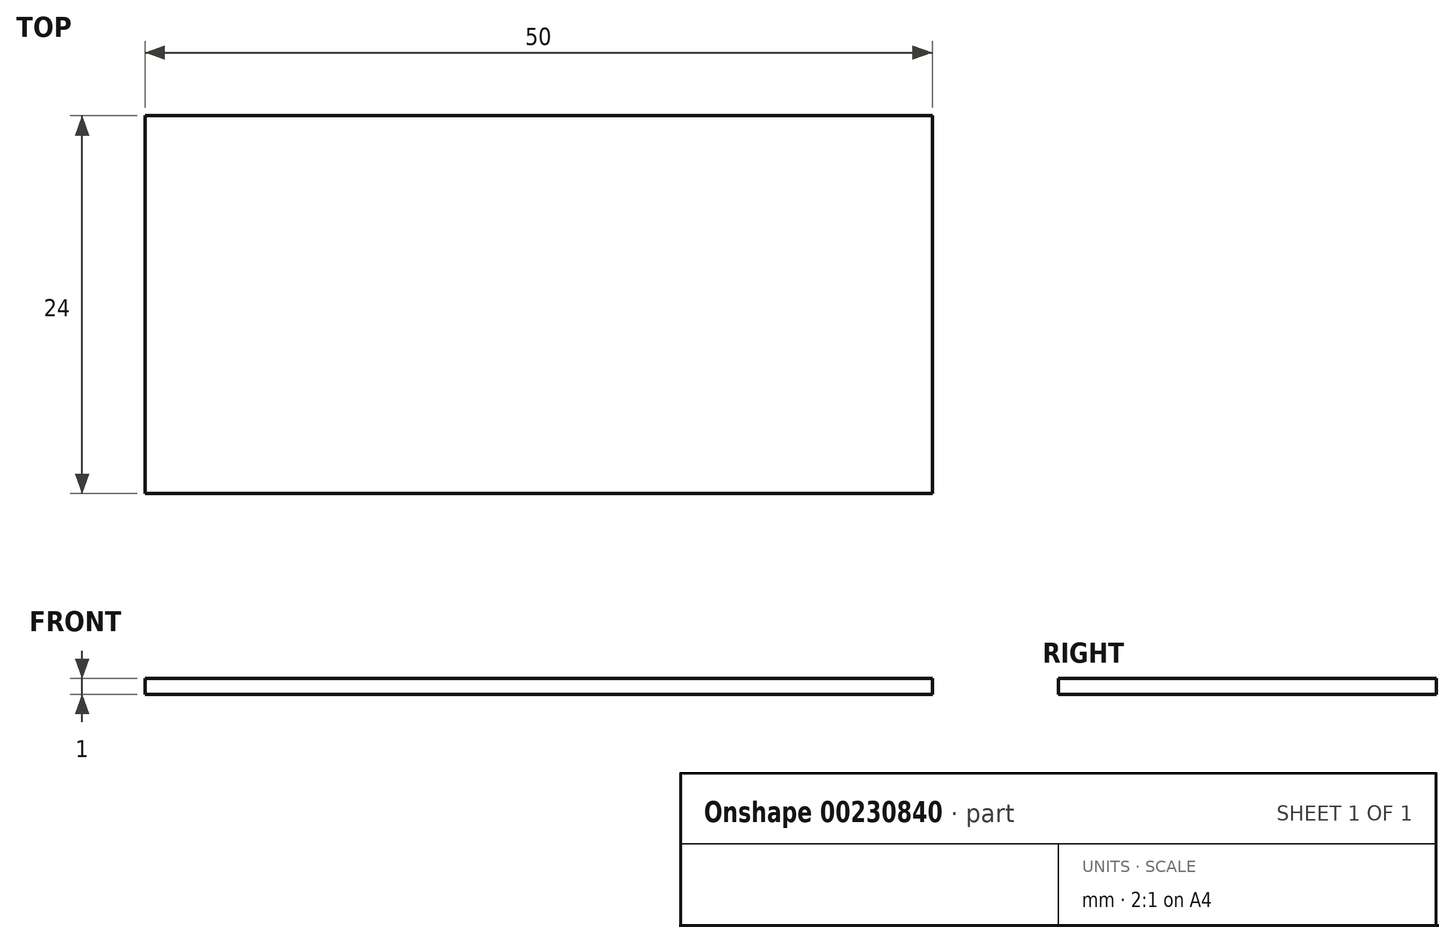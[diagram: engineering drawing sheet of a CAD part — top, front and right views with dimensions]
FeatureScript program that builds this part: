
annotation { "Feature Type Name" : "Feature", "Feature Type Description" : "" }
export const myFeature = defineFeature(function(context is Context, id is Id, definition is map)
    precondition{}
    {
        {
            var Q0;
            Q0=qCreatedBy(makeId("Top.planeOp"),FACE);
            var sketch = newSketch(context, id + "F0", { "sketchPlane" : qUnion([Q0])});
            skLineSegment(sketch, "E0.bottom", {"start": v(0, 0) * mm, "end": v(50, 0) * mm});
            skLineSegment(sketch, "E0.top", {"start": v(0, 24) * mm, "end": v(50, 24) * mm});
            skLineSegment(sketch, "E0.left", {"start": v(0, 0) * mm, "end": v(0, 24) * mm});
            skLineSegment(sketch, "E0.right", {"start": v(50, 0) * mm, "end": v(50, 24) * mm});
            skSolve(sketch);
        }
        {
            var Q0;
            Q0 = qSketchRegion(id + "F0", true);
            extrude(context, id + "F1", {"entities" : qUnion([Q0]), "depth" : 1 * mm});
        }
    });
